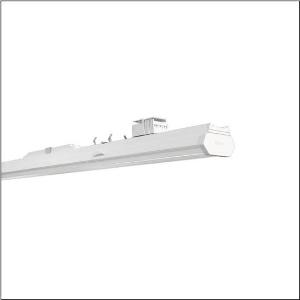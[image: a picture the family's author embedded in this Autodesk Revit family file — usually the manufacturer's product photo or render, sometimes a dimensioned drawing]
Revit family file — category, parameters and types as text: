
# Revit family: licross_r__11_protected_ho_51tp11cn4exs_0205
name_source: partatom
category: Lighting Fixtures
units: mm (PartAtom-declared; Revit-internal decimal feet)

## family parameters
Cut with Voids When Loaded = No
Host = Face
Light Source = No
Part Type = Normal
Room Calculation Point = No
Round Connector Dimension = Use Diameter
Shared = No

## types (1)
- --- (1 x LED, 14460 lm, 77.6 W, 4000K)
    Apparent Load = 78 VA
    CIE Flux Codes = 84 94 98 99 100
    Color Rendering = 80
    Color Temperature = 4000K
    Default Elevation = 1800 mm
    Description = Licross® 11 Protected HO, luminaire insert, of sheet steel, galvanised, coil coated, white, length: 1.500mm, width: 90mm, height: 101mm, LED rated luminous flux: 14.460lm, light colour: 840, control gear: ON/OFF Multilumen, CLOi, with plug, 3-pole, with phase selection, mains connection: 220..240V, AC, 50/60Hz, start of lifetime: 78W, end of service life: 87W, halogen-free wiring, primary light control with lens, of plastic, primary optical cover: cover, of PMMA, light emission: direct distribution, primary light characteristic: symmetric, protection rating (complete): IP64, insulation class (complete): insulation class I (protective earthing), certification: CE, ENEC, VDE, UKCA, protection symbol: D if used in an environment with conductive dust loads with corresponding accessories, impact resistance: IK06, permissible ambient temperature for indoor applications: -35..+35°C, corresponds to IFS (International Featured Standards) requirements for safety and quality in the food industry, reducing of maximum allowable ambient temperature of 5°C with ceiling mounting, LABS conformity tested according to VDMA 24364:2018-05, packaging unit: 1 piece
    Height = 92 mm
    Lamp = 1 x LED
    Lamp Light Flux = 14460 lm
    Lamp Power = 77.6 W
    Lamp count = 1
    Length = 1500 mm
    Luminous efficacy = 186 lm/W
    Manufacturer = Siteco
    ModVariant = No
    Model = 51TP11CN4EXS
    Mounting Place = Ceiling
    Mounting Type = Pendant
    Number of Poles = 1
    OnlyDefault = Yes
    Power Factor = 1
    Product Name = Licross® 11 Protected HO
    Product group = luminaire insert
    ProductGroupID = 901
    Protection Class = Protection class I
    Protection Degree = IP 64
    RLX_Detail_Level = 1
    RLX_Emergency_Light_Flux = 0 lm
    RLX_Emergency_Type = 0
    RLX_Emergency_Type_DB = No
    RlxData = <blob elided: 22093 chars, md5=42e20a3f>
    Socket = socket
    Standby Power = 0 W
    System Light Flux = 14460 lm
    System Power = 78 W
    Type Comments = factory setting: luminous flux: 100 % | (A | C | E) | 181 mA
    Type Image = l_1256148.jpg
    URL = http://relux.com
    VarID = @adj_038009
    Voltage = 0 V
    Weight = 0.00 kg
    Width = 88 mm

## geometry (parser evidence)
native form markers: Blend x4, Sweep x9
no freeform markers — native parametric forms only
